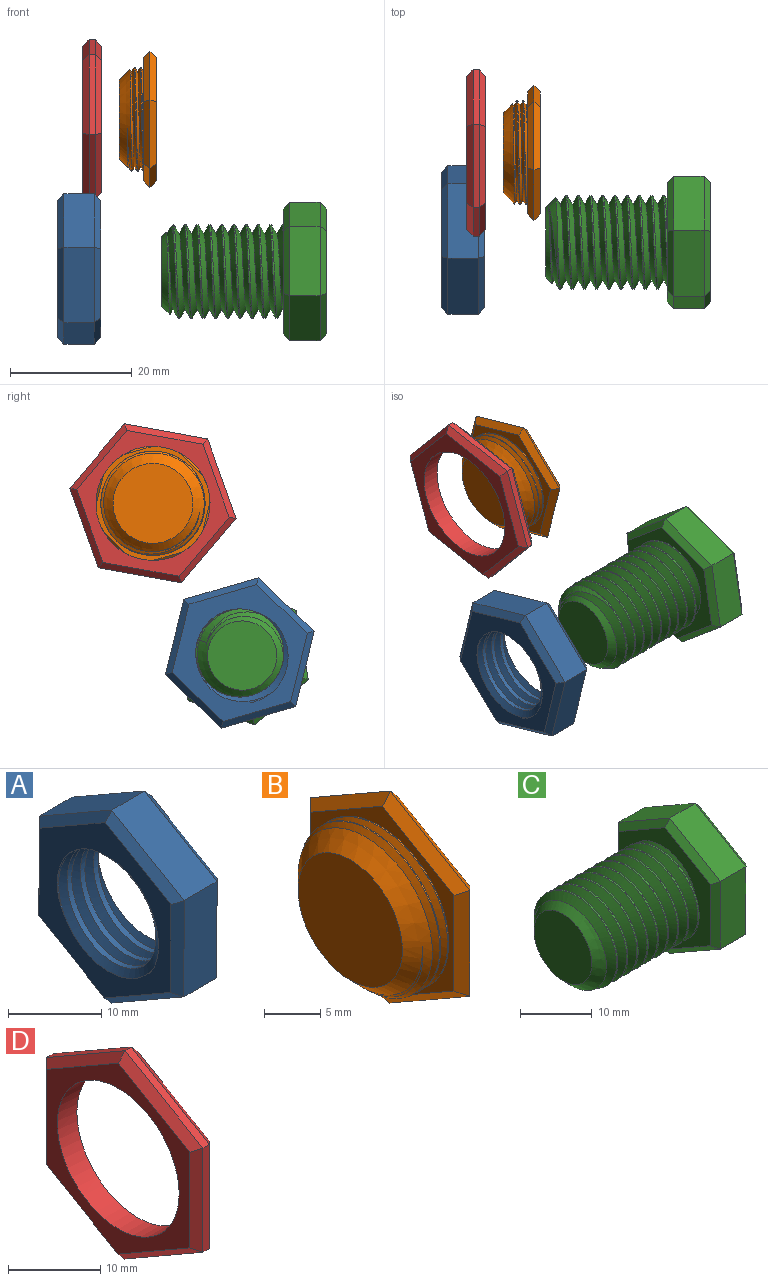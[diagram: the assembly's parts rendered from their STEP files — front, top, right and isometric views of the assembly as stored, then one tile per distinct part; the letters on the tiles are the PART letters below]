
ASSEMBLY  parts=4 mates=2
PART A: 23 faces, bbox 9.3x22.7x26 mm
  f0: cylinder r=7.24mm len=14.48mm, axis (1,0,0), area 111.6mm2, adj f7,f8,f21,f22
  f1: plane 10.98x6.38mm, normal (0,-0.5,0.86), area 63.5mm2, adj f2,f6,f14,f18
  f2: plane 12.7x5mm, normal (0,-1,0), area 63.5mm2, adj f1,f3,f12,f16
  f3: plane 11.02x6.32mm, normal (0,-0.5,-0.87), area 63.5mm2, adj f2,f4,f10,f15
  f4: plane 10.98x6.38mm, normal (0,0.5,-0.86), area 63.5mm2, adj f3,f5,f9,f17
  f5: plane 12.7x5mm, normal (0,1,0), area 63.5mm2, adj f4,f6,f11,f19
  f6: plane 11.02x6.32mm, normal (0,0.5,0.87), area 63.5mm2, adj f1,f5,f13,f20
  f7: plane 23.73x20.67mm, normal (-1,0,0), area 164.4mm2, adj f0,f9,f10,f11,f12,f13,f14,f21
  f8: plane 23.73x20.67mm, normal (1,0,0), area 164.4mm2, adj f0,f15,f16,f17,f18,f19,f20,f21
  f9: plane 10.99x6.96mm, normal (-0.71,0.36,-0.61), area 17.1mm2, adj f4,f7,f10,f11
  f10: plane 11.02x6.9mm, normal (-0.71,-0.35,-0.61), area 17.1mm2, adj f3,f7,f9,f12
  f11: plane 12.7x1.03mm, normal (-0.71,0.71,0), area 17.1mm2, adj f5,f7,f9,f13
  f12: plane 12.7x1.03mm, normal (-0.71,-0.71,0), area 17.1mm2, adj f2,f7,f10,f14
  f13: plane 11.02x6.9mm, normal (-0.71,0.35,0.61), area 17.1mm2, adj f6,f7,f11,f14
  f14: plane 10.99x6.96mm, normal (-0.71,-0.36,0.61), area 17.1mm2, adj f1,f7,f12,f13
  f15: plane 11.02x6.9mm, normal (0.71,-0.35,-0.61), area 17.1mm2, adj f3,f8,f16,f17
  f16: plane 12.7x1.03mm, normal (0.71,-0.71,0), area 17.1mm2, adj f2,f8,f15,f18
  f17: plane 10.99x6.96mm, normal (0.71,0.36,-0.61), area 17.1mm2, adj f4,f8,f15,f19
  f18: plane 10.99x6.96mm, normal (0.71,-0.36,0.61), area 17.1mm2, adj f1,f8,f16,f20
  f19: plane 12.7x1.03mm, normal (0.71,0.71,0), area 17.1mm2, adj f5,f8,f17,f20
  f20: plane 11.02x6.9mm, normal (0.71,0.35,0.61), area 17.1mm2, adj f6,f8,f18,f19
  f21: bspline ~19.31x16.73mm, area 223mm2, adj f0,f7,f8,f22
  f22: bspline ~19.31x16.73mm, area 223mm2, adj f0,f7,f8,f21
PART B: 20 faces, bbox 6x20.1x23.1 mm
  f0: cylinder r=8.55mm len=17.1mm, axis (1,0,0), area 13.4mm2, adj f1,f2,f4,f5,f7
  f1: bspline ~19.75x17.1mm, area 106.5mm2, adj f0,f2,f4,f5,f7
  f2: bspline ~19.75x17.1mm, area 106.6mm2, adj f0,f1,f4,f7
  f3: plane 13.1x13.1mm, normal (-1,0,0), area 134.8mm2, adj f4
  f4: cone r=8.55mm half-angle=45deg, axis (1,0,0), area 109.4mm2, adj f0,f1,f2,f3,f5
  f5: cone r=8.55mm half-angle=45deg, axis (1,0,0), area 0.4mm2, adj f0,f1,f4
  f6: plane 20.78x18.04mm, normal (1,0,0), area 280.6mm2, adj f8,f9,f10,f11,f12,f13
  f7: plane 20.8x18.06mm, normal (-1,0,0), area 68.2mm2, adj f0,f1,f2,f14,f15,f16,f17,f18
  f8: plane 9.98x6.38mm, normal (0.71,0.36,-0.61), area 15.5mm2, adj f6,f9,f10,f16
  f9: plane 10.02x6.32mm, normal (0.71,-0.35,-0.61), area 15.5mm2, adj f6,f8,f11,f14
  f10: plane 11.55x1.04mm, normal (0.71,0.71,0), area 15.5mm2, adj f6,f8,f12,f18
  f11: plane 11.55x1.04mm, normal (0.71,-0.71,0), area 15.5mm2, adj f6,f9,f13,f15
  f12: plane 10.02x6.32mm, normal (0.71,0.35,0.61), area 15.5mm2, adj f6,f10,f13,f19
  f13: plane 9.98x6.38mm, normal (0.71,-0.36,0.61), area 15.5mm2, adj f6,f11,f12,f17
  f14: plane 10.02x6.32mm, normal (-0.71,-0.35,-0.61), area 15.5mm2, adj f7,f9,f15,f16
  f15: plane 11.55x1.04mm, normal (-0.71,-0.71,0), area 15.5mm2, adj f7,f11,f14,f17
  f16: plane 9.98x6.38mm, normal (-0.71,0.36,-0.61), area 15.5mm2, adj f7,f8,f14,f18
  f17: plane 9.98x6.38mm, normal (-0.71,-0.36,0.61), area 15.5mm2, adj f7,f13,f15,f19
  f18: plane 11.55x1.04mm, normal (-0.71,0.71,0), area 15.5mm2, adj f7,f10,f16,f19
  f19: plane 10.02x6.32mm, normal (-0.71,0.35,0.61), area 15.5mm2, adj f7,f12,f17,f18
PART C: 26 faces, bbox 27.7x20x23.1 mm
  f0: cylinder r=7.68mm len=18mm, axis (1,0,0), area 139.1mm2, adj f1,f2,f5,f13
  f1: bspline ~20.88x17.74mm, area 713.8mm2, adj f0,f2,f4,f5,f13
  f2: bspline ~21.88x17.74mm, area 715.1mm2, adj f0,f1,f4,f5,f13
  f3: plane 11.36x11.36mm, normal (-1,0,0), area 101.4mm2, adj f4
  f4: cone r=7.68mm half-angle=45deg, axis (1,0,0), area 63.2mm2, adj f1,f2,f3,f5
  f5: cone r=7.68mm half-angle=45deg, axis (1,0,0), area 13.2mm2, adj f0,f1,f2,f4
  f6: plane 9.98x5.81mm, normal (0,-0.5,0.86), area 57.7mm2, adj f7,f11,f19,f23
  f7: plane 11.55x5mm, normal (0,-1,0), area 57.7mm2, adj f6,f8,f17,f21
  f8: plane 10.02x5.74mm, normal (0,-0.5,-0.87), area 57.7mm2, adj f7,f9,f15,f20
  f9: plane 9.98x5.81mm, normal (0,0.5,-0.86), area 57.7mm2, adj f8,f10,f14,f22
  f10: plane 11.55x5mm, normal (0,1,0), area 57.7mm2, adj f9,f11,f16,f24
  f11: plane 10.02x5.74mm, normal (0,0.5,0.87), area 57.7mm2, adj f6,f10,f18,f25
  f12: plane 20.78x18.04mm, normal (1,0,0), area 280.6mm2, adj f14,f15,f16,f17,f18,f19
  f13: plane 20.78x18.04mm, normal (-1,0,0), area 125.2mm2, adj f0,f1,f2,f20,f21,f22,f23,f24
  f14: plane 9.98x6.38mm, normal (0.71,0.36,-0.61), area 15.5mm2, adj f9,f12,f15,f16
  f15: plane 10.02x6.32mm, normal (0.71,-0.35,-0.61), area 15.5mm2, adj f8,f12,f14,f17
  f16: plane 11.55x1.04mm, normal (0.71,0.71,0), area 15.5mm2, adj f10,f12,f14,f18
  f17: plane 11.55x1.04mm, normal (0.71,-0.71,0), area 15.5mm2, adj f7,f12,f15,f19
  f18: plane 10.02x6.32mm, normal (0.71,0.35,0.61), area 15.5mm2, adj f11,f12,f16,f19
  f19: plane 9.98x6.38mm, normal (0.71,-0.36,0.61), area 15.5mm2, adj f6,f12,f17,f18
  f20: plane 10.02x6.32mm, normal (-0.71,-0.35,-0.61), area 15.5mm2, adj f8,f13,f21,f22
  f21: plane 11.55x1.04mm, normal (-0.71,-0.71,0), area 15.5mm2, adj f7,f13,f20,f23
  f22: plane 9.98x6.38mm, normal (-0.71,0.36,-0.61), area 15.5mm2, adj f9,f13,f20,f24
  f23: plane 9.98x6.38mm, normal (-0.71,-0.36,0.61), area 15.5mm2, adj f6,f13,f21,f25
  f24: plane 11.55x1.04mm, normal (-0.71,0.71,0), area 15.5mm2, adj f10,f13,f22,f25
  f25: plane 10.02x6.32mm, normal (-0.71,0.35,0.61), area 15.5mm2, adj f11,f13,f23,f24
PART D: 21 faces, bbox 3x24x27.7 mm
  f0: plane 11.99x6.95mm, normal (0,-0.5,0.87), area 13.9mm2, adj f1,f5,f13,f17
  f1: plane 13.86x1mm, normal (0,-1,0), area 13.9mm2, adj f0,f2,f11,f15
  f2: plane 12.01x6.91mm, normal (0,-0.5,-0.87), area 13.9mm2, adj f1,f3,f9,f14
  f3: plane 11.99x6.95mm, normal (0,0.5,-0.87), area 13.9mm2, adj f2,f4,f8,f16
  f4: plane 13.86x1mm, normal (0,1,0), area 13.9mm2, adj f3,f5,f10,f18
  f5: plane 12.01x6.91mm, normal (0,0.5,0.87), area 13.9mm2, adj f0,f4,f12,f19
  f6: plane 25.4x22.02mm, normal (-1,0,0), area 144.3mm2, adj f8,f9,f10,f11,f12,f13,f20
  f7: plane 25.4x22.02mm, normal (1,0,0), area 144.3mm2, adj f14,f15,f16,f17,f18,f19,f20
  f8: plane 11.99x7.53mm, normal (-0.71,0.35,-0.61), area 18.8mm2, adj f3,f6,f9,f10
  f9: plane 12.01x7.49mm, normal (-0.71,-0.35,-0.61), area 18.8mm2, adj f2,f6,f8,f11
  f10: plane 13.86x1.02mm, normal (-0.71,0.71,0), area 18.8mm2, adj f4,f6,f8,f12
  f11: plane 13.86x1.02mm, normal (-0.71,-0.71,0), area 18.8mm2, adj f1,f6,f9,f13
  f12: plane 12.01x7.49mm, normal (-0.71,0.35,0.61), area 18.8mm2, adj f5,f6,f10,f13
  f13: plane 11.99x7.53mm, normal (-0.71,-0.35,0.61), area 18.8mm2, adj f0,f6,f11,f12
  f14: plane 12.01x7.49mm, normal (0.71,-0.35,-0.61), area 18.8mm2, adj f2,f7,f15,f16
  f15: plane 13.86x1.02mm, normal (0.71,-0.71,0), area 18.8mm2, adj f1,f7,f14,f17
  f16: plane 11.99x7.53mm, normal (0.71,0.35,-0.61), area 18.8mm2, adj f3,f7,f14,f18
  f17: plane 11.99x7.53mm, normal (0.71,-0.35,0.61), area 18.8mm2, adj f0,f7,f15,f19
  f18: plane 13.86x1.02mm, normal (0.71,0.71,0), area 18.8mm2, adj f4,f7,f16,f19
  f19: plane 12.01x7.49mm, normal (0.71,0.35,0.61), area 18.8mm2, adj f5,f7,f17,f18
  f20: cylinder r=9.35mm len=18.71mm, axis (1,0,0), area 176.3mm2, adj f6,f7
PLACE A rot(axis=(0,0.6,-0.8),180deg) t=(-55.27,-6.86,23.48)mm fixed
PLACE B rot(axis=(1,0,0),13.8deg) t=(-40.16,7.38,48.02)mm
PLACE C rot(axis=(1,0,0),109.9deg) t=(-14.77,-7.25,23.06)mm
PLACE D rot(axis=(1,0,0),100.2deg) t=(-48.16,7.38,48.02)mm fixed
MATE cylindrical C.f0 <-> A.f7  axis (-1,0,0) through (-38.27,-7.25,23.06)mm
MATE cylindrical B.f0 <-> D.f20  axis (-1,0,0) through (-45.16,7.38,48.02)mm
